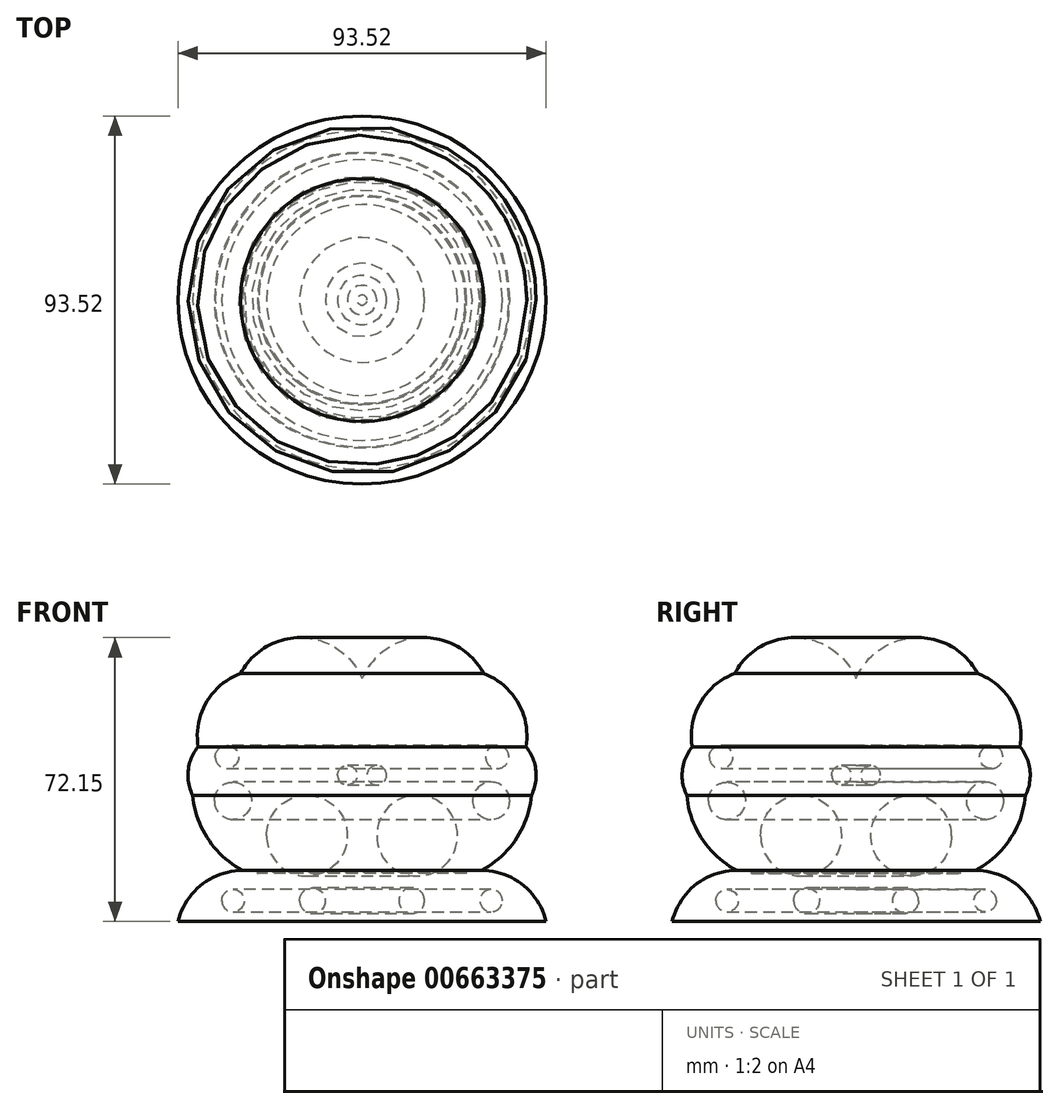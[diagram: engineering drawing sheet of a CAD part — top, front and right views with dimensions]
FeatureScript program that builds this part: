
annotation { "Feature Type Name" : "Feature", "Feature Type Description" : "" }
export const myFeature = defineFeature(function(context is Context, id is Id, definition is map)
    precondition{}
    {
        {
            var Q0;
            Q0=qCreatedBy(makeId("Front.planeOp"),FACE);
            var sketch = newSketch(context, id + "F0", { "sketchPlane" : qUnion([Q0])});
            skArc(sketch, "E0", {"start": v(-26.44, 12.51) * mm, "mid": v(-26.51, 12.36) * mm, "end": v(-26.58, 12.2) * mm});
            skLineSegment(sketch, "E1", {"start": v(0, 48.41) * mm, "end": v(0, 0) * mm});
            skLineSegment(sketch, "E2", {"start": v(-46.76, 0) * mm, "end": v(0, 0) * mm});
            skArc(sketch, "E3", {"start": v(-43.03, 32.07) * mm, "mid": v(-39.1, 20.92) * mm, "end": v(-30.34, 12.97) * mm});
            skArc(sketch, "E4", {"start": v(-41.63, 44.42) * mm, "mid": v(-44.15, 38.45) * mm, "end": v(-43.03, 32.07) * mm});
            skArc(sketch, "E5", {"start": v(-30.86, 63.02) * mm, "mid": v(-23.05, 39.62) * mm, "end": v(0, 48.41) * mm});
            skArc(sketch, "E6", {"start": v(-30.86, 63.02) * mm, "mid": v(-39.6, 55.66) * mm, "end": v(-41.63, 44.42) * mm});
            skPoint(sketch, "E7.orphan", {"position": v(-55.2, 0) * mm});
            skArc(sketch, "E8.trimOffspring", {"start": v(-30.34, 12.97) * mm, "mid": v(-40.8, 9.34) * mm, "end": v(-46.76, 0) * mm});
            skArc(sketch, "E9.trimOffspring", {"start": v(-26.25, 12.47) * mm, "mid": v(-26.42, 12.34) * mm, "end": v(-26.58, 12.2) * mm});
            skArc(sketch, "E10.trimOffspring", {"start": v(-26.25, 12.47) * mm, "mid": v(-26.35, 12.5) * mm, "end": v(-26.44, 12.51) * mm});
            skCircle(sketch, "E11", {"center": v(-14, 21.82) * mm, "radius": 10.26 * mm});
            skCircle(sketch, "E12", {"center": v(-32.8, 30.68) * mm, "radius": 4.73 * mm});
            skCircle(sketch, "E13", {"center": v(-32.8, 5.3) * mm, "radius": 2.84 * mm});
            skCircle(sketch, "E14", {"center": v(-12.6, 5.3) * mm, "radius": 3.27 * mm});
            skCircle(sketch, "E15", {"center": v(-3.74, 37.17) * mm, "radius": 2.47 * mm});
            skCircle(sketch, "E16", {"center": v(-34.33, 41.8) * mm, "radius": 2.96 * mm});
            skSolve(sketch);
        }
        {
            var Q0;
            Q0=makeQuery(id+"F0.imprint","IMPRINT",FACE,{"disambiguationData":[TD([[makeQuery(id+"F0.imprint","IMPRINT",EDGE,{"derivedFrom":sQuery(id+"F0.wireOp",EDGE,"E0")}),-1.0]])]});
            var Q1;
            Q1=sQuery(id+"F0.wireOp",EDGE,"E1");
            revolve(context, id + "F1", {"entities" : qUnion([Q0]), "axis" : qUnion([Q1]), "revolveType" : RevolveType.FULL});
        }
    });
